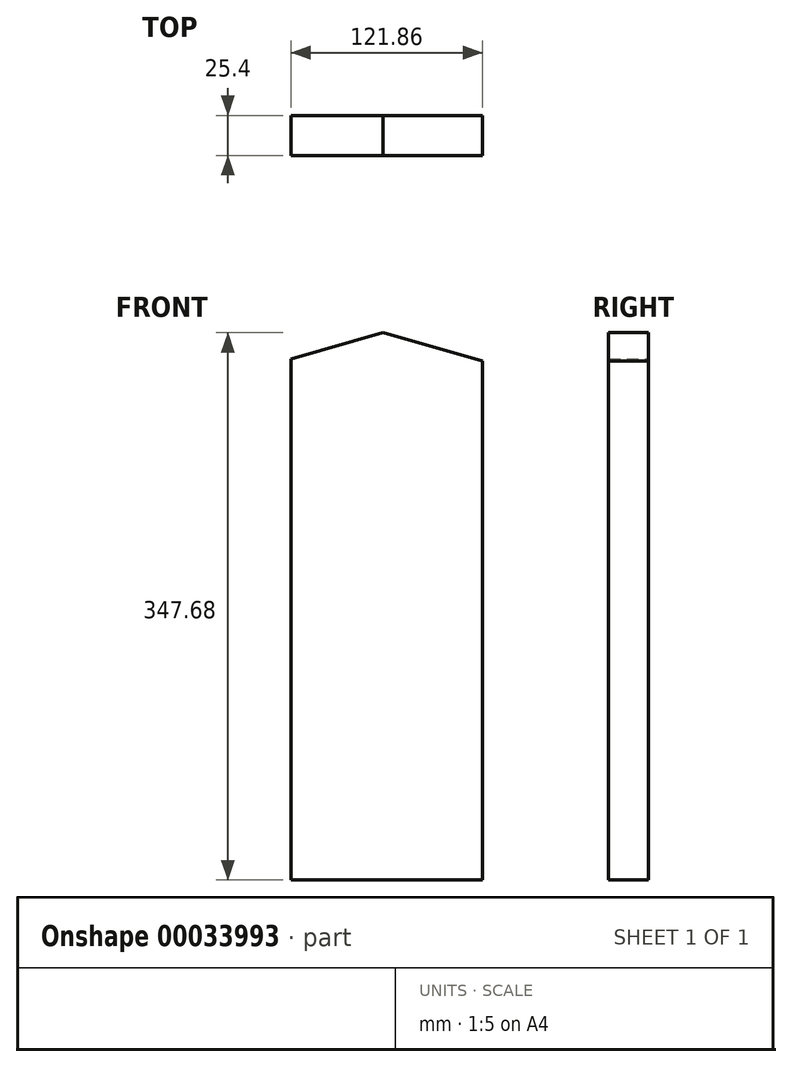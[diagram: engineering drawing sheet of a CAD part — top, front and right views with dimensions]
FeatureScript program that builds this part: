
annotation { "Feature Type Name" : "Feature", "Feature Type Description" : "" }
export const myFeature = defineFeature(function(context is Context, id is Id, definition is map)
    precondition{}
    {
        {
            var Q0;
            Q0=qCreatedBy(makeId("Front.planeOp"),FACE);
            var sketch = newSketch(context, id + "F0", { "sketchPlane" : qUnion([Q0])});
            skLineSegment(sketch, "E0", {"start": v(-61.4, 129.92) * mm, "end": v(-2.75, 146.68) * mm});
            skLineSegment(sketch, "E1", {"start": v(-2.75, 146.68) * mm, "end": v(60.47, 128.61) * mm});
            skLineSegment(sketch, "E2", {"start": v(60.47, 128.61) * mm, "end": v(60.47, -201) * mm});
            skLineSegment(sketch, "E3", {"start": v(60.47, -201) * mm, "end": v(-61.4, -201) * mm});
            skLineSegment(sketch, "E4", {"start": v(-61.4, -201) * mm, "end": v(-61.4, 129.92) * mm});
            skSolve(sketch);
        }
        {
            var Q0;
            Q0=makeQuery(id+"F0.imprint","IMPRINT",FACE,{"disambiguationData":[TD([[makeQuery(id+"F0.imprint","IMPRINT",EDGE,{"derivedFrom":sQuery(id+"F0.wireOp",EDGE,"E0")}),-1.0]])]});
            extrude(context, id + "F1", {"entities" : qUnion([Q0]), "depth" : 25.4 * mm});
        }
    });
